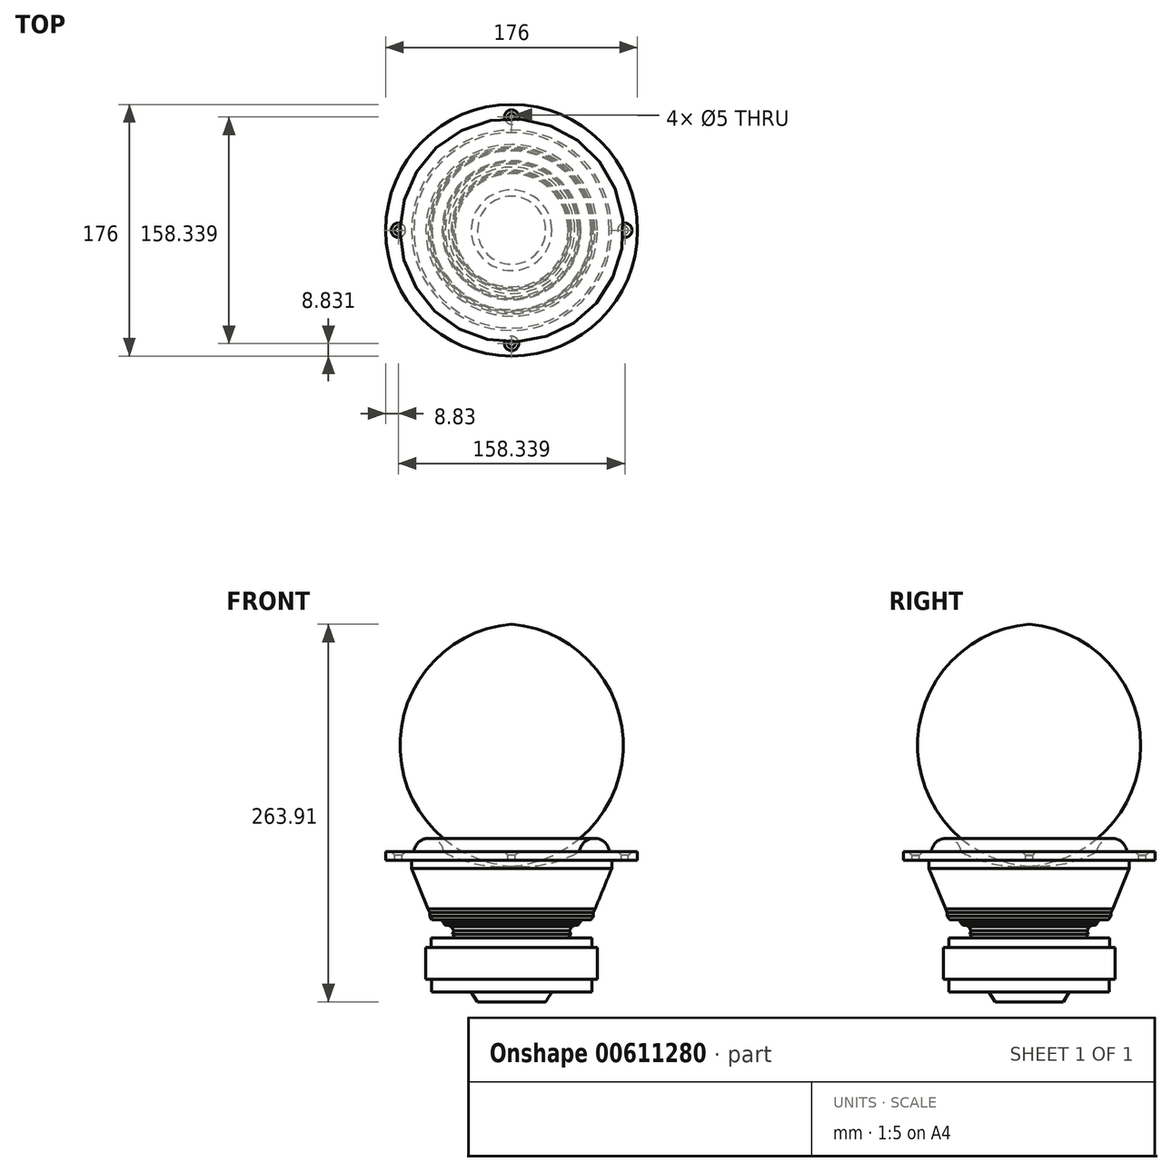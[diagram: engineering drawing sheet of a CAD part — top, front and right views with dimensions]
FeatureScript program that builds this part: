
annotation { "Feature Type Name" : "Feature", "Feature Type Description" : "" }
export const myFeature = defineFeature(function(context is Context, id is Id, definition is map)
    precondition{}
    {
        {
            var Q0;
            Q0=qCreatedBy(makeId("Front.planeOp"),FACE);
            var sketch = newSketch(context, id + "F0", { "sketchPlane" : qUnion([Q0])});
            skCircle(sketch, "E0", {"center": v(0, 0) * mm, "radius": 88.25 * mm});
            skLineSegment(sketch, "E1", {"start": v(-238.51, 74.17) * mm, "end": v(-238.51, -84.71) * mm});
            skLineSegment(sketch, "E2", {"start": v(-214.71, -47.29) * mm, "end": v(-210.32, -40.44) * mm});
            skLineSegment(sketch, "E3", {"start": v(-210.32, -40.44) * mm, "end": v(-182.52, -40.44) * mm});
            skLineSegment(sketch, "E4", {"start": v(-182.52, -40.44) * mm, "end": v(-182.52, -31.5) * mm});
            skLineSegment(sketch, "E5", {"start": v(-182.52, -31.5) * mm, "end": v(-178.51, -31.5) * mm});
            skLineSegment(sketch, "E6", {"start": v(-178.51, -9.34) * mm, "end": v(-182.28, -9.34) * mm});
            skLineSegment(sketch, "E7", {"start": v(-182.28, -9.34) * mm, "end": v(-182.28, -2.75) * mm});
            skLineSegment(sketch, "E8", {"start": v(-199, -2.75) * mm, "end": v(-197.09, 0) * mm});
            skLineSegment(sketch, "E9", {"start": v(-197.09, 0) * mm, "end": v(-198.07, 2.47) * mm});
            skLineSegment(sketch, "E10", {"start": v(-198.07, 2.47) * mm, "end": v(-196.39, 5.34) * mm});
            skLineSegment(sketch, "E11", {"start": v(-196.39, 5.34) * mm, "end": v(-194.36, 6.25) * mm});
            skLineSegment(sketch, "E12", {"start": v(-194.36, 6.25) * mm, "end": v(-192.19, 6.25) * mm});
            skLineSegment(sketch, "E13", {"start": v(-192.19, 6.25) * mm, "end": v(-190.5, 8.5) * mm});
            skLineSegment(sketch, "E14", {"start": v(-190.5, 8.5) * mm, "end": v(-189.94, 9.96) * mm});
            skLineSegment(sketch, "E15", {"start": v(-189.94, 9.96) * mm, "end": v(-183, 9.96) * mm});
            skLineSegment(sketch, "E16", {"start": v(-183, 9.96) * mm, "end": v(-181.26, 12.49) * mm});
            skLineSegment(sketch, "E17", {"start": v(-181.26, 12.49) * mm, "end": v(-181.26, 15.29) * mm});
            skLineSegment(sketch, "E18", {"start": v(-181.26, 15.29) * mm, "end": v(-180.14, 17.74) * mm});
            skLineSegment(sketch, "E19", {"start": v(-180.14, 17.74) * mm, "end": v(-168.51, 45.83) * mm});
            skLineSegment(sketch, "E20", {"start": v(-168.51, 51.71) * mm, "end": v(-150.51, 51.71) * mm});
            skLineSegment(sketch, "E21", {"start": v(-150.51, 57.6) * mm, "end": v(-170.2, 57.6) * mm});
            skArc(sketch, "E22", {"start": v(-170.2, 57.6) * mm, "mid": v(-180.6, 67.04) * mm, "end": v(-191, 57.6) * mm});
            skLineSegment(sketch, "E23", {"start": v(-199, -2.75) * mm, "end": v(-182.28, -2.75) * mm});
            skLineSegment(sketch, "E24.0", {"start": v(-178.51, -9.34) * mm, "end": v(-178.51, -31.5) * mm});
            skLineSegment(sketch, "E25.0", {"start": v(-168.51, 51.71) * mm, "end": v(-168.51, 45.83) * mm});
            skLineSegment(sketch, "E26.0", {"start": v(-150.51, 57.6) * mm, "end": v(-150.51, 51.71) * mm});
            skArc(sketch, "E27", {"start": v(-238.51, 47.47) * mm, "mid": v(-214.01, 49.06) * mm, "end": v(-191, 57.6) * mm});
            skPoint(sketch, "E28.orphan", {"position": v(-246.51, -56.23) * mm});
            skLineSegment(sketch, "E29.0", {"start": v(-238.51, -47.29) * mm, "end": v(-214.71, -47.29) * mm});
            skSolve(sketch);
        }
        {
            var Q0;
            Q0=makeQuery(id+"F0.imprint","IMPRINT",FACE,{"disambiguationData":[TD([[makeQuery(id+"F0.imprint","IMPRINT",EDGE,{"derivedFrom":sQuery(id+"F0.wireOp",EDGE,"E2")}),1.0]])]});
            var Q1;
            Q1=sQuery(id+"F0.wireOp",EDGE,"E1");
            revolve(context, id + "F1", {"entities" : qUnion([Q0]), "axis" : qUnion([Q1]), "revolveType" : RevolveType.FULL});
        }
        {
            var Q0;
            Q0=makeQuery(id+"F1.opRevolve","SWEPT_FACE",FACE,{"disambiguationData":[OSD([sQuery(id+"F0.wireOp",EDGE,"E21")])]});
            var sketch = newSketch(context, id + "F2", { "sketchPlane" : qUnion([Q0])});
            skLineSegment(sketch, "E30", {"start": v(-159.34, 0) * mm, "end": v(-317.68, 0) * mm});
            skLineSegment(sketch, "E31", {"start": v(-238.51, -79.17) * mm, "end": v(-238.51, 79.17) * mm});
            skPoint(sketch, "E32.orphan", {"position": v(-238.51, 0) * mm});
            skCircle(sketch, "E33", {"center": v(-238.51, 0) * mm, "radius": 79.17 * mm});
            skPoint(sketch, "E34.orphan", {"position": v(-150.51, 0) * mm});
            skPoint(sketch, "E35.orphan", {"position": v(-326.51, 0) * mm});
            skSolve(sketch);
        }
        {
            var Q0;
            Q0=sQuery(id+"F2.wireOp",VERTEX,"E31.end");
            var Q1;
            Q1=sQuery(id+"F2.wireOp",VERTEX,"E30.end");
            var Q2;
            Q2=sQuery(id+"F2.wireOp",VERTEX,"E30.start");
            var Q3;
            Q3=sQuery(id+"F2.wireOp",VERTEX,"E31.start");
            var Q4;
            Q4=makeQuery(id+"F1.opRevolve","SWEPT_BODY",BODY,{"disambiguationData":[OSD([sQuery(id+"F0.wireOp",EDGE,"E1"),sQuery(id+"F0.wireOp",EDGE,"E2"),sQuery(id+"F0.wireOp",EDGE,"E3"),sQuery(id+"F0.wireOp",EDGE,"E4"),sQuery(id+"F0.wireOp",EDGE,"E5"),sQuery(id+"F0.wireOp",EDGE,"E6"),sQuery(id+"F0.wireOp",EDGE,"E7"),sQuery(id+"F0.wireOp",EDGE,"E8"),sQuery(id+"F0.wireOp",EDGE,"E9"),sQuery(id+"F0.wireOp",EDGE,"E10"),sQuery(id+"F0.wireOp",EDGE,"E11"),sQuery(id+"F0.wireOp",EDGE,"E12"),sQuery(id+"F0.wireOp",EDGE,"E13"),sQuery(id+"F0.wireOp",EDGE,"E14"),sQuery(id+"F0.wireOp",EDGE,"E15"),sQuery(id+"F0.wireOp",EDGE,"E16"),sQuery(id+"F0.wireOp",EDGE,"E17"),sQuery(id+"F0.wireOp",EDGE,"E18"),sQuery(id+"F0.wireOp",EDGE,"E19"),sQuery(id+"F0.wireOp",EDGE,"E20"),sQuery(id+"F0.wireOp",EDGE,"E21"),sQuery(id+"F0.wireOp",EDGE,"E22"),sQuery(id+"F0.wireOp",EDGE,"E23"),sQuery(id+"F0.wireOp",EDGE,"E24.0"),sQuery(id+"F0.wireOp",EDGE,"E25.0"),sQuery(id+"F0.wireOp",EDGE,"E26.0"),sQuery(id+"F0.wireOp",EDGE,"E27"),sQuery(id+"F0.wireOp",EDGE,"E29.0")])]});
            hole(context, id + "F3", {"style" : HoleStyle.C_SINK, "endStyle" : HoleEndStyle.THROUGH, "holeDiameter" : 5 * mm, "cSinkDiameter" : 10 * mm, "cSinkAngle" : 90 * degree, "majorDiameter" : 5 * mm, "isTappedThrough" : true, "tappedDepth" : 12 * mm, "tapClearance" : 3, "startFromSketch" : true, "locations" : qUnion([Q0, Q1, Q2, Q3]), "scope" : qUnion([Q4])});
        }
    });
